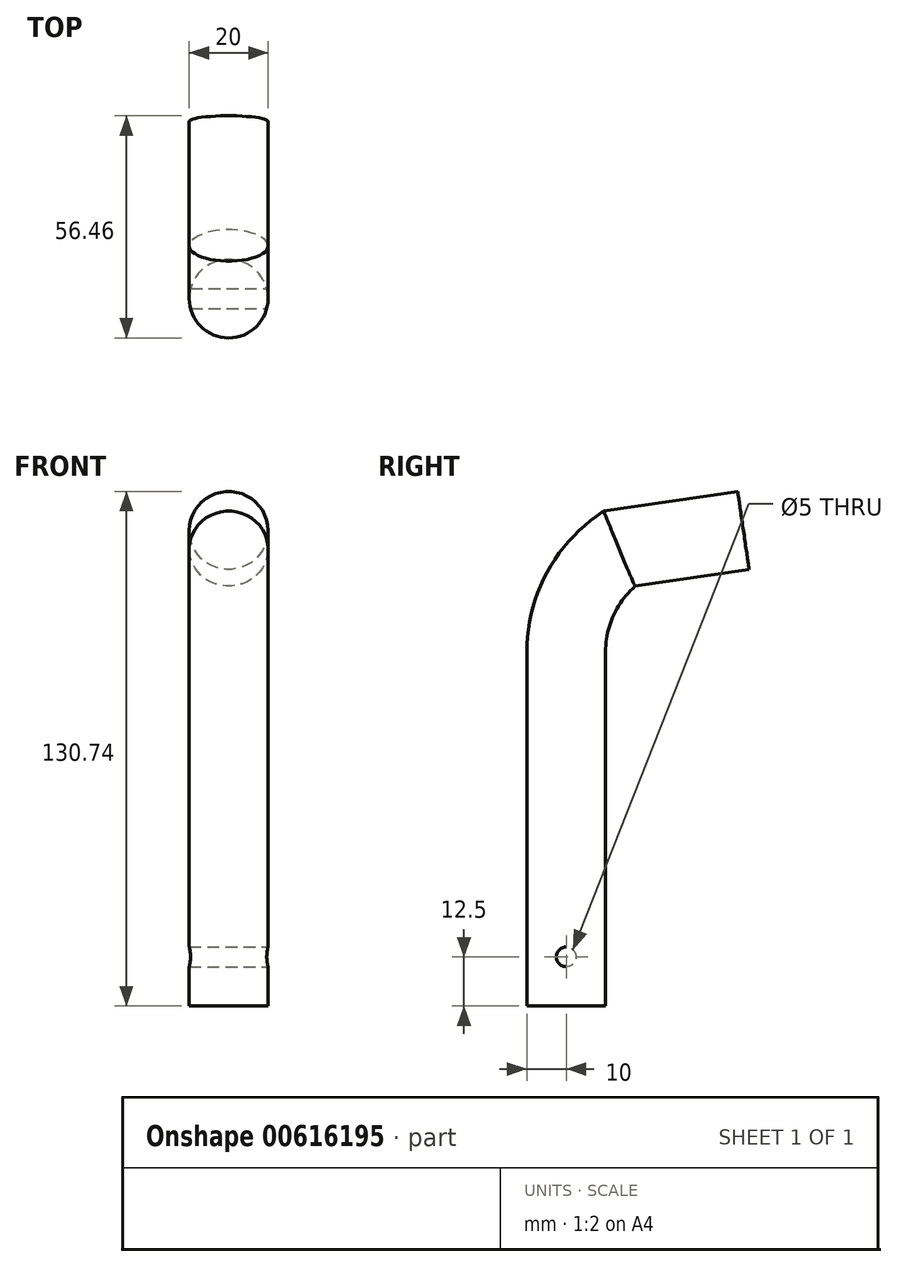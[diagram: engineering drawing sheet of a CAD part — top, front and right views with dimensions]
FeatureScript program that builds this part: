
annotation { "Feature Type Name" : "Feature", "Feature Type Description" : "" }
export const myFeature = defineFeature(function(context is Context, id is Id, definition is map)
    precondition{}
    {
        {
            var Q0;
            Q0=qCreatedBy(makeId("Top.planeOp"),FACE);
            var sketch = newSketch(context, id + "F0", { "sketchPlane" : qUnion([Q0])});
            skCircle(sketch, "E0", {"center": v(0, 0) * mm, "radius": 10 * mm});
            skSolve(sketch);
        }
        {
            var Q0;
            Q0=qCreatedBy(makeId("Right.planeOp"),FACE);
            var sketch = newSketch(context, id + "F1", { "sketchPlane" : qUnion([Q0])});
            skLineSegment(sketch, "E1", {"start": v(0, 0) * mm, "end": v(0, 32.5) * mm});
            skLineSegment(sketch, "E2", {"start": v(0, 0) * mm, "end": v(0, -32.5) * mm});
            skArc(sketch, "E3", {"start": v(13.4, 58.71) * mm, "mid": v(3.54, 47.22) * mm, "end": v(0, 32.5) * mm});
            skLineSegment(sketch, "E4", {"start": v(13.4, 58.71) * mm, "end": v(45.01, 63.34) * mm});
            skSolve(sketch);
        }
        {
            var Q0;
            Q0=makeQuery(id+"F0.imprint","IMPRINT",FACE,{"disambiguationData":[TD([[makeQuery(id+"F0.imprint","IMPRINT",EDGE,{"derivedFrom":sQuery(id+"F0.wireOp",EDGE,"E0")}),1.0]])]});
            var Q1;
            Q1=sQuery(id+"F1.wireOp",EDGE,"E3");
            var Q2;
            Q2=sQuery(id+"F1.wireOp",EDGE,"E4");
            var Q3;
            Q3=sQuery(id+"F1.wireOp",EDGE,"E1");
            var Q4;
            Q4=sQuery(id+"F1.wireOp",EDGE,"E2");
            sweep(context, id + "F2", {"profiles" : qUnion([Q0]), "path" : qUnion([Q1, Q2, Q3, Q4])});
        }
        {
            var Q0;
            Q0=makeQuery(id+"F2.opSweep","CAP_FACE",FACE,{"disambiguationData":[OSD([sQuery(id+"F0.wireOp",EDGE,"E0"),sQuery(id+"F1.wireOp",VERTEX,"E2.end")])],"isStart":true});
            var sketch = newSketch(context, id + "F3", { "sketchPlane" : qUnion([Q0])});
            skCircle(sketch, "E5", {"center": v(0, 0) * mm, "radius": 10 * mm});
            skSolve(sketch);
        }
        {
            var Q0;
            Q0=makeQuery(id+"F3.imprint","IMPRINT",FACE,{"disambiguationData":[TD([[makeQuery(id+"F3.imprint","IMPRINT",EDGE,{"derivedFrom":sQuery(id+"F3.wireOp",EDGE,"E5")}),-1.0]])]});
            extrude(context, id + "F4", {"entities" : qUnion([Q0]), "operationType" : NewBodyOperationType.ADD, "depth" : 25 * mm, "offsetDistance" : 25 * mm});
        }
        {
            var Q0;
            Q0=qCreatedBy(makeId("Right.planeOp"),FACE);
            var sketch = newSketch(context, id + "F5", { "sketchPlane" : qUnion([Q0])});
            skCircle(sketch, "E6", {"center": v(0, -45) * mm, "radius": 2.5 * mm});
            skSolve(sketch);
        }
        {
            var Q0;
            Q0=makeQuery(id+"F5.imprint","IMPRINT",FACE,{"disambiguationData":[TD([[makeQuery(id+"F5.imprint","IMPRINT",EDGE,{"derivedFrom":sQuery(id+"F5.wireOp",EDGE,"E6")}),1.0]])]});
            var Q1;
            Q1=sQuery(id+"F5.wireOp",EDGE,"E6");
            extrude(context, id + "F6", {"entities" : qUnion([Q0]), "operationType" : NewBodyOperationType.REMOVE, "surfaceEntities" : qUnion([Q1]), "oppositeDirection" : true, "depth" : 25 * mm, "offsetDistance" : 25 * mm});
        }
        {
            var Q0;
            Q0=makeQuery(id+"F6.boolean.opBoolean","COPY",FACE,{"derivedFrom":makeQuery(id+"F6.opExtrude","CAP_FACE",FACE,{"disambiguationData":[OSD([sQuery(id+"F5.wireOp",EDGE,"E6")])],"isStart":true})});
            extrude(context, id + "F7", {"entities" : qUnion([Q0]), "operationType" : NewBodyOperationType.REMOVE, "oppositeDirection" : true, "depth" : 25 * mm, "offsetDistance" : 25 * mm});
        }
    });
